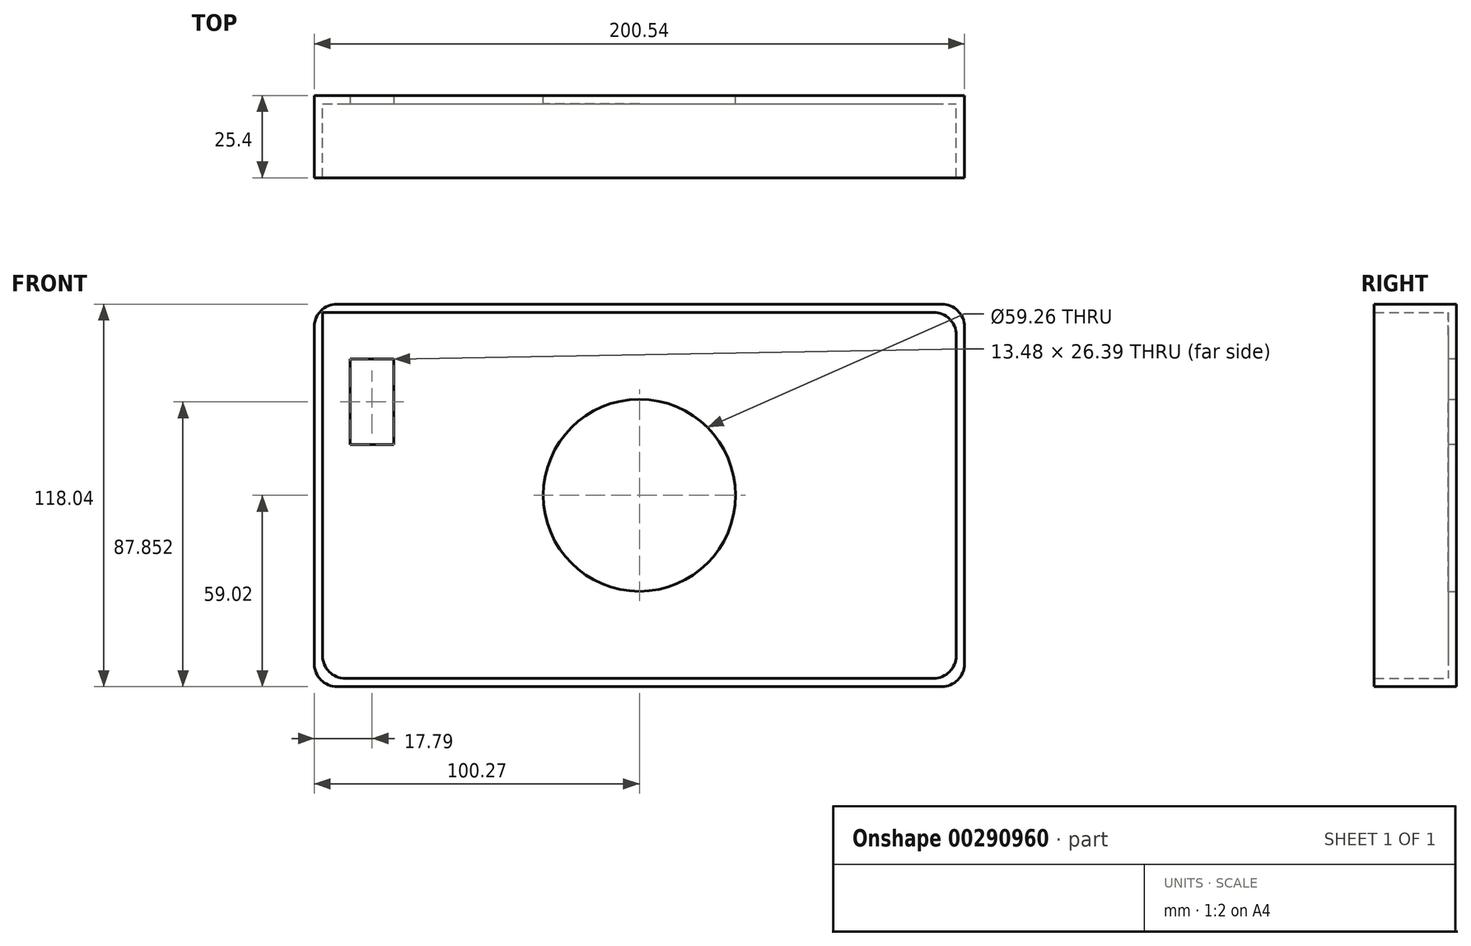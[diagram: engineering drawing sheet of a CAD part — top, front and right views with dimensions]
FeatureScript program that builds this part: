
annotation { "Feature Type Name" : "Feature", "Feature Type Description" : "" }
export const myFeature = defineFeature(function(context is Context, id is Id, definition is map)
    precondition{}
    {
        {
            var Q0;
            Q0=qCreatedBy(makeId("Front.planeOp"),FACE);
            var sketch = newSketch(context, id + "F0", { "sketchPlane" : qUnion([Q0])});
            skLineSegment(sketch, "E0.bottom", {"start": v(-100.27, 59.02) * mm, "end": v(100.27, 59.02) * mm});
            skLineSegment(sketch, "E0.top", {"start": v(-100.27, -59.02) * mm, "end": v(100.27, -59.02) * mm});
            skLineSegment(sketch, "E0.left", {"start": v(-100.27, 59.02) * mm, "end": v(-100.27, -59.02) * mm});
            skLineSegment(sketch, "E0.right", {"start": v(100.27, 59.02) * mm, "end": v(100.27, -59.02) * mm});
            skPoint(sketch, "E0.middle", {"position": v(0, 0) * mm});
            skSolve(sketch);
        }
        {
            var Q0;
            Q0=makeQuery(id+"F0.imprint","IMPRINT",FACE,{"disambiguationData":[TD([[makeQuery(id+"F0.imprint","IMPRINT",EDGE,{"derivedFrom":sQuery(id+"F0.wireOp",EDGE,"E0.bottom")}),-1.0]])]});
            extrude(context, id + "F1", {"entities" : qUnion([Q0]), "depth" : 25.4 * mm});
        }
        {
            var Q0;
            Q0=makeQuery(id+"F1.opExtrude","CAP_FACE",FACE,{"disambiguationData":[OSD([sQuery(id+"F0.wireOp",EDGE,"E0.bottom"),sQuery(id+"F0.wireOp",EDGE,"E0.top"),sQuery(id+"F0.wireOp",EDGE,"E0.left"),sQuery(id+"F0.wireOp",EDGE,"E0.right")])],"isStart":false});
            shell(context, id + "F2", {"entities" : qUnion([Q0]), "thickness" : 2.54 * mm});
        }
        {
            var Q0;
            Q0=makeQuery(id+"F1.opExtrude","SWEPT_EDGE",EDGE,{"disambiguationData":[OSD([sQuery(id+"F0.wireOp",EDGE,"E0.bottom"),sQuery(id+"F0.wireOp",EDGE,"E0.left")])]});
            var Q1;
            Q1=makeQuery(id+"F1.opExtrude","SWEPT_EDGE",EDGE,{"disambiguationData":[OSD([sQuery(id+"F0.wireOp",EDGE,"E0.bottom"),sQuery(id+"F0.wireOp",EDGE,"E0.right")])]});
            var Q2;
            Q2=makeQuery(id+"F1.opExtrude","SWEPT_EDGE",EDGE,{"disambiguationData":[OSD([sQuery(id+"F0.wireOp",EDGE,"E0.top"),sQuery(id+"F0.wireOp",EDGE,"E0.right")])]});
            var Q3;
            Q3=makeQuery(id+"F1.opExtrude","SWEPT_EDGE",EDGE,{"disambiguationData":[OSD([sQuery(id+"F0.wireOp",EDGE,"E0.top"),sQuery(id+"F0.wireOp",EDGE,"E0.left")])]});
            var Q4;
            Q4=makeQuery(id+"F2.opShell","OFFSET_EDGE",EDGE,{"disambiguationData":[OSD([sQuery(id+"F0.wireOp",EDGE,"E0.bottom"),sQuery(id+"F0.wireOp",EDGE,"E0.right")])]});
            var Q5;
            Q5=makeQuery(id+"F2.opShell","OFFSET_EDGE",EDGE,{"disambiguationData":[OSD([sQuery(id+"F0.wireOp",EDGE,"E0.top"),sQuery(id+"F0.wireOp",EDGE,"E0.right")])]});
            var Q6;
            Q6=makeQuery(id+"F2.opShell","OFFSET_EDGE",EDGE,{"disambiguationData":[OSD([sQuery(id+"F0.wireOp",EDGE,"E0.top"),sQuery(id+"F0.wireOp",EDGE,"E0.left")])]});
            fillet(context, id + "F3", {"entities" : qUnion([Q0, Q1, Q2, Q3, Q4, Q5, Q6]), "radius" : 7 * mm, "tangentPropagation" : true, "allowEdgeOverflow" : false});
        }
        {
            var Q0;
            Q0=makeQuery(id+"F2.opShell","OFFSET_FACE",FACE,{"disambiguationData":[OSD([sQuery(id+"F0.wireOp",EDGE,"E0.bottom"),sQuery(id+"F0.wireOp",EDGE,"E0.top"),sQuery(id+"F0.wireOp",EDGE,"E0.left"),sQuery(id+"F0.wireOp",EDGE,"E0.right")])]});
            var sketch = newSketch(context, id + "F4", { "sketchPlane" : qUnion([Q0])});
            skLineSegment(sketch, "E1.bottom", {"start": v(-89.22, 42.03) * mm, "end": v(-75.74, 42.03) * mm});
            skLineSegment(sketch, "E1.top", {"start": v(-89.22, 15.64) * mm, "end": v(-75.74, 15.64) * mm});
            skLineSegment(sketch, "E1.left", {"start": v(-89.22, 42.03) * mm, "end": v(-89.22, 15.64) * mm});
            skLineSegment(sketch, "E1.right", {"start": v(-75.74, 42.03) * mm, "end": v(-75.74, 15.64) * mm});
            skSolve(sketch);
        }
        {
            var Q0;
            Q0=makeQuery(id+"F4.imprint","IMPRINT",FACE,{"disambiguationData":[TD([[makeQuery(id+"F4.imprint","IMPRINT",EDGE,{"derivedFrom":sQuery(id+"F4.wireOp",EDGE,"E1.bottom")}),-1.0]])]});
            extrude(context, id + "F5", {"entities" : qUnion([Q0]), "operationType" : NewBodyOperationType.REMOVE, "oppositeDirection" : true, "depth" : 25 * mm});
        }
        {
            var Q0;
            Q0=makeQuery(id+"F1.opExtrude","CAP_FACE",FACE,{"disambiguationData":[OSD([sQuery(id+"F0.wireOp",EDGE,"E0.bottom"),sQuery(id+"F0.wireOp",EDGE,"E0.top"),sQuery(id+"F0.wireOp",EDGE,"E0.left"),sQuery(id+"F0.wireOp",EDGE,"E0.right")])],"isStart":true});
            var sketch = newSketch(context, id + "F6", { "sketchPlane" : qUnion([Q0])});
            skCircle(sketch, "E2", {"center": v(0, 0) * mm, "radius": 29.63 * mm});
            skSolve(sketch);
        }
        {
            var Q0;
            Q0 = qSketchRegion(id + "F6", true);
            extrude(context, id + "F7", {"entities" : qUnion([Q0]), "operationType" : NewBodyOperationType.REMOVE, "oppositeDirection" : true, "depth" : 25 * mm});
        }
    });
